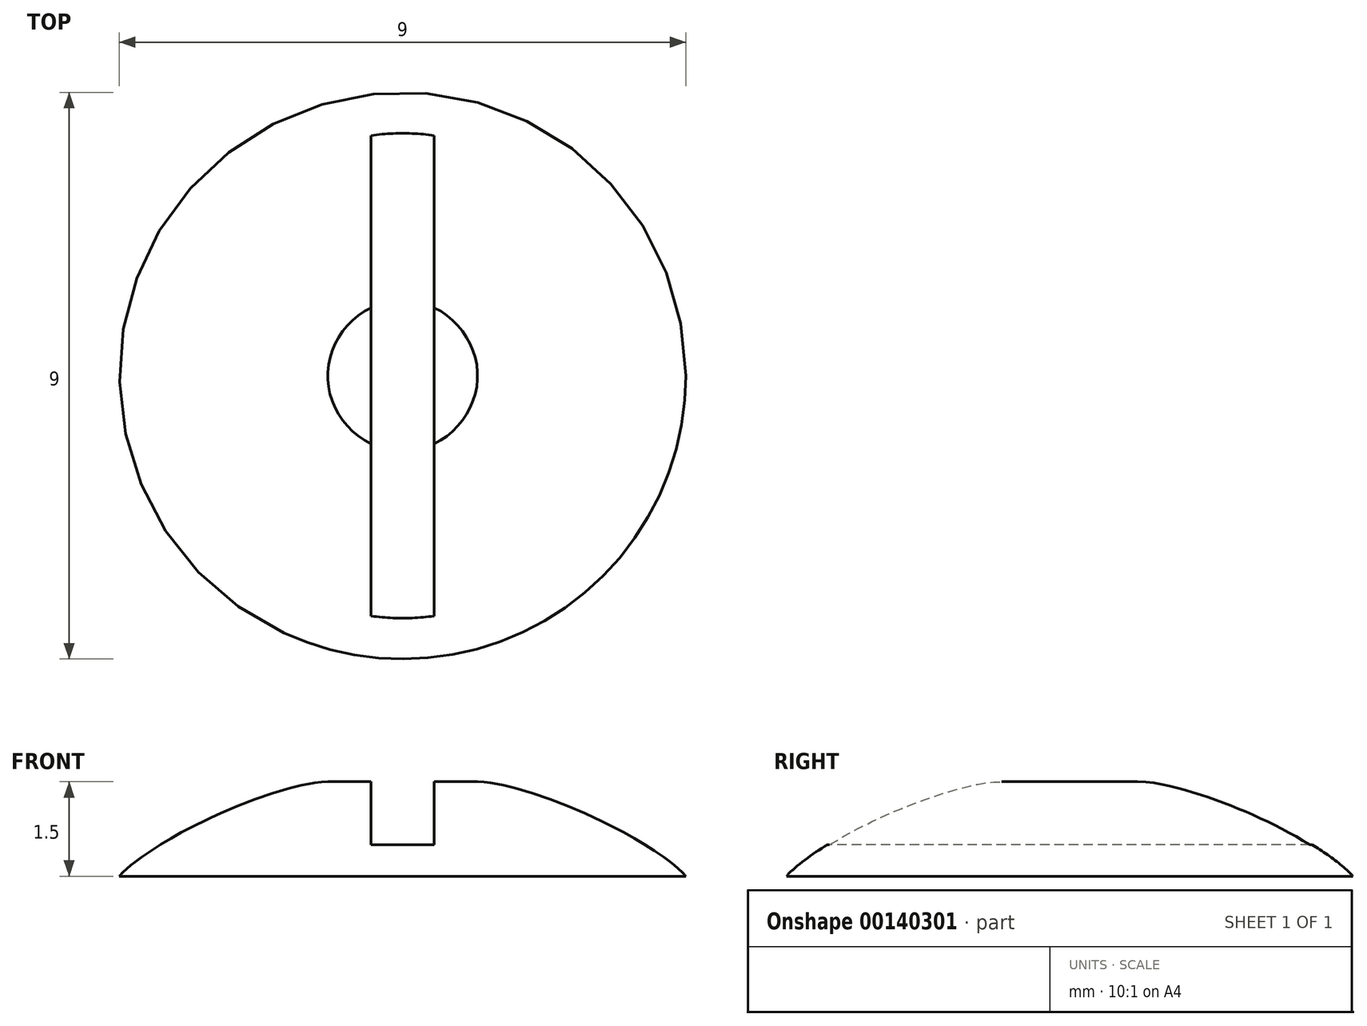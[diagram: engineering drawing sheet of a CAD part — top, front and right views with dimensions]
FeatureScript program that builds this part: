
annotation { "Feature Type Name" : "Feature", "Feature Type Description" : "" }
export const myFeature = defineFeature(function(context is Context, id is Id, definition is map)
    precondition{}
    {
        {
            var Q0;
            Q0=qCreatedBy(makeId("Top.planeOp"),FACE);
            var sketch = newSketch(context, id + "F0", { "sketchPlane" : qUnion([Q0])});
            skCircle(sketch, "E0", {"center": v(0, 0) * mm, "radius": 4.5 * mm});
            skSolve(sketch);
        }
        {
            var Q0;
            Q0=makeQuery(id+"F0.imprint","IMPRINT",FACE,{"disambiguationData":[TD([[makeQuery(id+"F0.imprint","IMPRINT",EDGE,{"derivedFrom":sQuery(id+"F0.wireOp",EDGE,"E0")}),1.0]])]});
            var sketch = newSketch(context, id + "F1", { "sketchPlane" : qUnion([Q0])});
            skLineSegment(sketch, "E1", {"start": v(-0.5, 7.5) * mm, "end": v(-0.5, -7.5) * mm});
            skLineSegment(sketch, "E2", {"start": v(0.5, 7.5) * mm, "end": v(0.5, -7.5) * mm});
            skLineSegment(sketch, "E3", {"start": v(-0.5, -7.5) * mm, "end": v(0.5, -7.5) * mm});
            skLineSegment(sketch, "E4", {"start": v(0.5, 7.5) * mm, "end": v(-0.5, 7.5) * mm});
            skLineSegment(sketch, "E5", {"start": v(0, -7.5) * mm, "end": v(0, 0) * mm, "construction": true});
            skLineSegment(sketch, "E6", {"start": v(0, 0) * mm, "end": v(0.5, 0) * mm, "construction": true});
            skSolve(sketch);
        }
        {
            var Q0;
            Q0=makeQuery(id+"F0.imprint","IMPRINT",FACE,{"disambiguationData":[TD([[makeQuery(id+"F0.imprint","IMPRINT",EDGE,{"derivedFrom":sQuery(id+"F0.wireOp",EDGE,"E0")}),1.0]])]});
            extrude(context, id + "F2", {"entities" : qUnion([Q0]), "depth" : 1 * mm, "hasSecondDirection" : true, "secondDirectionOppositeDirection" : true, "secondDirectionDepth" : 0.5 * mm});
        }
        {
            var Q0;
            Q0=makeQuery(id+"F2.opExtrude","CAP_EDGE",EDGE,{"disambiguationData":[OSD([sQuery(id+"F0.wireOp",EDGE,"E0")])],"isStart":false});
            fillet(context, id + "F3", {"entities" : qUnion([Q0]), "radius" : 4.4 * mm, "tangentPropagation" : true, "rho" : 0.3, "crossSection" : FilletCrossSection.CONIC, "allowEdgeOverflow" : false});
        }
        {
            var Q0;
            {var subQ0=sQuery(id+"F1.wireOp",EDGE,"E4");Q0=makeQuery(id+"F1.imprint","IMPRINT",FACE,{"disambiguationData":[TD([[makeQuery(id+"F1.imprint","IMPRINT",EDGE,{"derivedFrom":subQ0}),1.0]])]});}
            var Q1;
            {var subQ0=sQuery(id+"F1.wireOp",EDGE,"E1");var subQ1=makeQuery(id+"F0.imprint","IMPRINT",EDGE,{"derivedFrom":sQuery(id+"F0.wireOp",EDGE,"E0")});var subQ2=makeQuery(id+"F1.imprint","INTERSECT",VERTEX,{"disambiguationData":[OD(0.0)],"derivedFrom":[subQ1,subQ0]});Q1=makeQuery(id+"F1.imprint","IMPRINT",FACE,{"disambiguationData":[TD([[makeQuery(id+"F1.imprint","IMPRINT",EDGE,{"disambiguationData":[TD([[subQ2,-1.0]])],"derivedFrom":subQ0}),1.0]])]});}
            var Q2;
            {var subQ0=sQuery(id+"F1.wireOp",EDGE,"E3");Q2=makeQuery(id+"F1.imprint","IMPRINT",FACE,{"disambiguationData":[TD([[makeQuery(id+"F1.imprint","IMPRINT",EDGE,{"derivedFrom":subQ0}),1.0]])]});}
            extrude(context, id + "F4", {"entities" : qUnion([Q0, Q1, Q2]), "operationType" : NewBodyOperationType.REMOVE, "endBound" : BoundingType.THROUGH_ALL, "depth" : 25 * mm});
        }
    });
